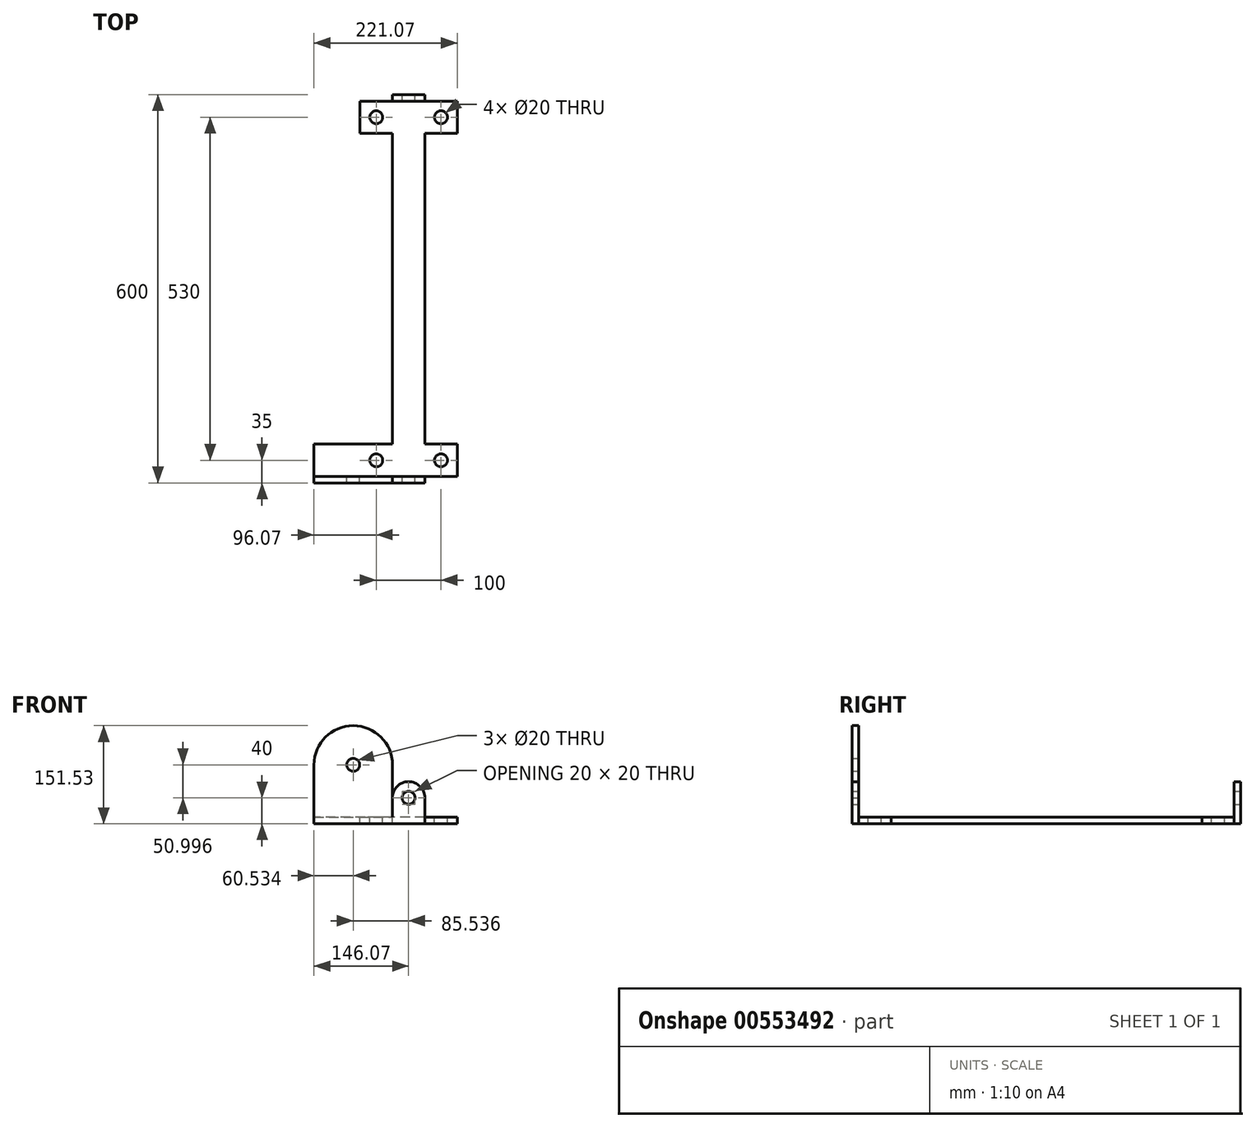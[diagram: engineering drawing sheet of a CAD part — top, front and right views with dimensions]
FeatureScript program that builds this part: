
annotation { "Feature Type Name" : "Feature", "Feature Type Description" : "" }
export const myFeature = defineFeature(function(context is Context, id is Id, definition is map)
    precondition{}
    {
        {
            var Q0;
            Q0=qCreatedBy(makeId("Front.planeOp"),FACE);
            var sketch = newSketch(context, id + "F0", { "sketchPlane" : qUnion([Q0])});
            skLineSegment(sketch, "E0.bottom", {"start": v(0, 0) * mm, "end": v(50, 0) * mm});
            skLineSegment(sketch, "E0.top", {"start": v(0, 40) * mm, "end": v(25, 40) * mm});
            skLineSegment(sketch, "E0.left", {"start": v(0, 0) * mm, "end": v(0, 40) * mm});
            skLineSegment(sketch, "E0.right", {"start": v(50, 0) * mm, "end": v(50, 40) * mm});
            skArc(sketch, "E1", {"start": v(50, 40) * mm, "mid": v(25, 65) * mm, "end": v(0, 40) * mm});
            skSolve(sketch);
        }
        {
            var Q0;
            Q0=qSketchRegion(id+"F0",true);
            extrude(context, id + "F1", {"entities" : qUnion([Q0]), "depth" : 10 * mm});
        }
        {
            var Q0;
            Q0=makeQuery(id+"F1.opExtrude","CAP_FACE",FACE,{"disambiguationData":[OSD([sQuery(id+"F0.wireOp",EDGE,"E0.bottom"),sQuery(id+"F0.wireOp",EDGE,"E0.left"),sQuery(id+"F0.wireOp",EDGE,"E0.right"),sQuery(id+"F0.wireOp",EDGE,"E1")])],"isStart":true});
            var sketch = newSketch(context, id + "F2", { "sketchPlane" : qUnion([Q0])});
            skLineSegment(sketch, "E2", {"start": v(-25, 0) * mm, "end": v(-25, 65) * mm, "construction": true});
            skLineSegment(sketch, "E3", {"start": v(-50, 40) * mm, "end": v(0, 40) * mm, "construction": true});
            skCircle(sketch, "E4", {"center": v(-25, 40) * mm, "radius": 10 * mm});
            skSolve(sketch);
        }
        {
            var Q0;
            Q0=qSketchRegion(id+"F2",true);
            extrude(context, id + "F3", {"entities" : qUnion([Q0]), "operationType" : NewBodyOperationType.REMOVE, "oppositeDirection" : true, "depth" : 25 * mm});
        }
        {
            var Q0;
            Q0=makeQuery(id+"F1.opExtrude","CAP_FACE",FACE,{"disambiguationData":[OSD([sQuery(id+"F0.wireOp",EDGE,"E0.bottom"),sQuery(id+"F0.wireOp",EDGE,"E0.left"),sQuery(id+"F0.wireOp",EDGE,"E0.right"),sQuery(id+"F0.wireOp",EDGE,"E1")])],"isStart":true});
            var sketch = newSketch(context, id + "F4", { "sketchPlane" : qUnion([Q0])});
            skLineSegment(sketch, "E5.bottom", {"start": v(-50, 0) * mm, "end": v(0, 0) * mm});
            skLineSegment(sketch, "E5.top", {"start": v(-50, 10) * mm, "end": v(0, 10) * mm});
            skLineSegment(sketch, "E5.left", {"start": v(-50, 0) * mm, "end": v(-50, 10) * mm});
            skLineSegment(sketch, "E5.right", {"start": v(0, 0) * mm, "end": v(0, 10) * mm});
            skSolve(sketch);
        }
        {
            var Q0;
            Q0=qSketchRegion(id+"F4",true);
            extrude(context, id + "F5", {"entities" : qUnion([Q0]), "depth" : 580 * mm});
        }
        {
            var Q0;
            Q0=makeQuery(id+"F1.opExtrude","SWEPT_BODY",BODY,{"disambiguationData":[OSD([sQuery(id+"F0.wireOp",EDGE,"E0.bottom"),sQuery(id+"F0.wireOp",EDGE,"E0.left"),sQuery(id+"F0.wireOp",EDGE,"E0.right"),sQuery(id+"F0.wireOp",EDGE,"E1")])]});
            transform(context, id + "F6", {"entities" : qUnion([Q0]), "transformType" : TransformType.TRANSLATION_3D, "dx" : 0 * mm, "dy" : 590 * mm, "dz" : 0 * mm, "makeCopy" : true});
        }
        {
            var Q0;
            Q0=makeQuery(id+"F1.opExtrude","CAP_FACE",FACE,{"disambiguationData":[OSD([sQuery(id+"F0.wireOp",EDGE,"E0.bottom"),sQuery(id+"F0.wireOp",EDGE,"E0.left"),sQuery(id+"F0.wireOp",EDGE,"E0.right"),sQuery(id+"F0.wireOp",EDGE,"E1")])],"isStart":false});
            var sketch = newSketch(context, id + "F7", { "sketchPlane" : qUnion([Q0])});
            skCircle(sketch, "E6", {"center": v(25, 0) * mm, "radius": 10 * mm});
            skSolve(sketch);
        }
        {
            var Q0;
            Q0=qSketchRegion(id+"F7",true);
            extrude(context, id + "F8", {"entities" : qUnion([Q0]), "oppositeDirection" : true, "depth" : 40 * mm});
        }
        {
            var Q0;
            Q0=makeQuery(id+"F8.opExtrude","SWEPT_BODY",BODY,{"disambiguationData":[OSD([sQuery(id+"F7.wireOp",EDGE,"E6")])]});
            transform(context, id + "F9", {"entities" : qUnion([Q0]), "transformType" : TransformType.TRANSLATION_3D, "dx" : 0 * mm, "dy" : 560 * mm, "dz" : 0 * mm, "makeCopy" : true});
        }
        {
            var Q0;
            Q0=makeQuery(id+"F8.opExtrude","SWEPT_BODY",BODY,{"disambiguationData":[OSD([sQuery(id+"F7.wireOp",EDGE,"E6")])]});
            deleteBodies(context, id + "F10", {"entities" : qUnion([Q0])});
        }
        {
            var Q0;
            Q0=makeQuery(id+"F9.opPattern","COPY",BODY,{"derivedFrom":makeQuery(id+"F8.opExtrude","SWEPT_BODY",BODY,{"disambiguationData":[OSD([sQuery(id+"F7.wireOp",EDGE,"E6")])]}),"instanceName":"1"});
            deleteBodies(context, id + "F11", {"entities" : qUnion([Q0])});
        }
        {
            var Q0;
            Q0=makeQuery(id+"F5.opExtrude","SWEPT_FACE",FACE,{"disambiguationData":[OSD([sQuery(id+"F4.wireOp",EDGE,"E5.top")])]});
            var sketch = newSketch(context, id + "F12", { "sketchPlane" : qUnion([Q0])});
            skLineSegment(sketch, "E7", {"start": v(0, 290) * mm, "end": v(50, 290) * mm, "construction": true});
            skLineSegment(sketch, "E8", {"start": v(0, 0) * mm, "end": v(-50, 0) * mm});
            skLineSegment(sketch, "E9", {"start": v(-50, 0) * mm, "end": v(-50, 50) * mm});
            skLineSegment(sketch, "E10", {"start": v(-50, 50) * mm, "end": v(0, 50) * mm});
            skLineSegment(sketch, "E11", {"start": v(0, 50) * mm, "end": v(0, 0) * mm});
            skLineSegment(sketch, "E12.MirrorCS", {"start": v(0, 580) * mm, "end": v(-50, 580) * mm});
            skLineSegment(sketch, "E13.MirrorCS", {"start": v(0, 530) * mm, "end": v(0, 580) * mm});
            skLineSegment(sketch, "E14.MirrorCS", {"start": v(-50, 530) * mm, "end": v(0, 530) * mm});
            skLineSegment(sketch, "E15.MirrorCS", {"start": v(-50, 580) * mm, "end": v(-50, 530) * mm});
            skLineSegment(sketch, "E16", {"start": v(25, 0) * mm, "end": v(25, 105.3) * mm, "construction": true});
            skLineSegment(sketch, "E17.MirrorCS", {"start": v(100, 50) * mm, "end": v(50, 50) * mm});
            skLineSegment(sketch, "E18.MirrorCS", {"start": v(100, 0) * mm, "end": v(100, 50) * mm});
            skLineSegment(sketch, "E19.MirrorCS", {"start": v(50, 0) * mm, "end": v(100, 0) * mm});
            skLineSegment(sketch, "E20.MirrorCS", {"start": v(50, 50) * mm, "end": v(50, 0) * mm});
            skLineSegment(sketch, "E21.MirrorCS", {"start": v(50, 580) * mm, "end": v(100, 580) * mm});
            skLineSegment(sketch, "E22.MirrorCS", {"start": v(100, 580) * mm, "end": v(100, 530) * mm});
            skLineSegment(sketch, "E23.MirrorCS", {"start": v(100, 530) * mm, "end": v(50, 530) * mm});
            skLineSegment(sketch, "E24.MirrorCS", {"start": v(50, 530) * mm, "end": v(50, 580) * mm});
            skLineSegment(sketch, "E25", {"start": v(-50, 25) * mm, "end": v(0, 25) * mm, "construction": true});
            skLineSegment(sketch, "E26", {"start": v(-25, 50) * mm, "end": v(-25, 0) * mm, "construction": true});
            skCircle(sketch, "E27", {"center": v(-25, 25) * mm, "radius": 10 * mm});
            skCircle(sketch, "E28.MirrorC", {"center": v(75, 25) * mm, "radius": 10 * mm});
            skCircle(sketch, "E29.MirrorC", {"center": v(-25, 555) * mm, "radius": 10 * mm});
            skCircle(sketch, "E30.MirrorC", {"center": v(75, 555) * mm, "radius": 10 * mm});
            skSolve(sketch);
        }
        {
            var Q0;
            Q0=qSketchRegion(id+"F12",true);
            extrude(context, id + "F13", {"entities" : qUnion([Q0]), "operationType" : NewBodyOperationType.ADD, "oppositeDirection" : true, "depth" : 10 * mm});
        }
        {
            var Q0;
            Q0=makeQuery(id+"F13.boolean.opBoolean","MERGE",FACE,{"disambiguationData":[OD(0.0)],"derivedFrom":[makeQuery(id+"F5.opExtrude","CAP_FACE",FACE,{"disambiguationData":[OSD([sQuery(id+"F4.wireOp",EDGE,"E5.bottom"),sQuery(id+"F4.wireOp",EDGE,"E5.top"),sQuery(id+"F4.wireOp",EDGE,"E5.left"),sQuery(id+"F4.wireOp",EDGE,"E5.right")])],"isStart":true}),makeQuery(id+"F13.opExtrude","SWEPT_FACE",FACE,{"disambiguationData":[OSD([sQuery(id+"F12.wireOp",EDGE,"E8")])]}),makeQuery(id+"F13.opExtrude","SWEPT_FACE",FACE,{"disambiguationData":[OSD([sQuery(id+"F12.wireOp",EDGE,"E19.MirrorCS")])]})]});
            var sketch = newSketch(context, id + "F14", { "sketchPlane" : qUnion([Q0])});
            skLineSegment(sketch, "E31", {"start": v(-50, 0) * mm, "end": v(-121.07, 0) * mm});
            skLineSegment(sketch, "E32", {"start": v(-121.07, 0) * mm, "end": v(-121.07, 10) * mm});
            skLineSegment(sketch, "E33", {"start": v(-121.07, 10) * mm, "end": v(-50, 10) * mm});
            skLineSegment(sketch, "E34", {"start": v(-50, 10) * mm, "end": v(0, 10) * mm});
            skLineSegment(sketch, "E35", {"start": v(0, 10) * mm, "end": v(0, 0) * mm});
            skLineSegment(sketch, "E36", {"start": v(0, 0) * mm, "end": v(-50, 0) * mm});
            skLineSegment(sketch, "E37", {"start": v(-50, 10) * mm, "end": v(-50, 0) * mm});
            skLineSegment(sketch, "E38", {"start": v(-121.07, 10) * mm, "end": v(-121.07, 91) * mm});
            skLineSegment(sketch, "E39", {"start": v(-121.07, 91) * mm, "end": v(0, 91) * mm});
            skLineSegment(sketch, "E40", {"start": v(0, 91) * mm, "end": v(0, 10) * mm});
            skLineSegment(sketch, "E41", {"start": v(-60.54, 91) * mm, "end": v(-60.54, 112.8) * mm, "construction": true});
            skCircle(sketch, "E42", {"center": v(-60.54, 91) * mm, "radius": 60.54 * mm});
            skCircle(sketch, "E43", {"center": v(-60.54, 91) * mm, "radius": 10 * mm});
            skSolve(sketch);
        }
        {
            var Q0;
            Q0 = qSketchRegion(id + "F14", true);
            extrude(context, id + "F15", {"entities" : qUnion([Q0]), "operationType" : NewBodyOperationType.ADD, "depth" : 10 * mm, "offsetDistance" : 25 * mm});
        }
        {
            var Q0;
            Q0=makeQuery(id+"F14.imprint","IMPRINT",FACE,{"disambiguationData":[TD([[makeQuery(id+"F14.imprint","IMPRINT",EDGE,{"derivedFrom":sQuery(id+"F14.wireOp",EDGE,"E31")}),-1.0]])]});
            extrude(context, id + "F16", {"entities" : qUnion([Q0]), "operationType" : NewBodyOperationType.ADD, "oppositeDirection" : true, "depth" : 50 * mm, "offsetDistance" : 25 * mm});
        }
    });
